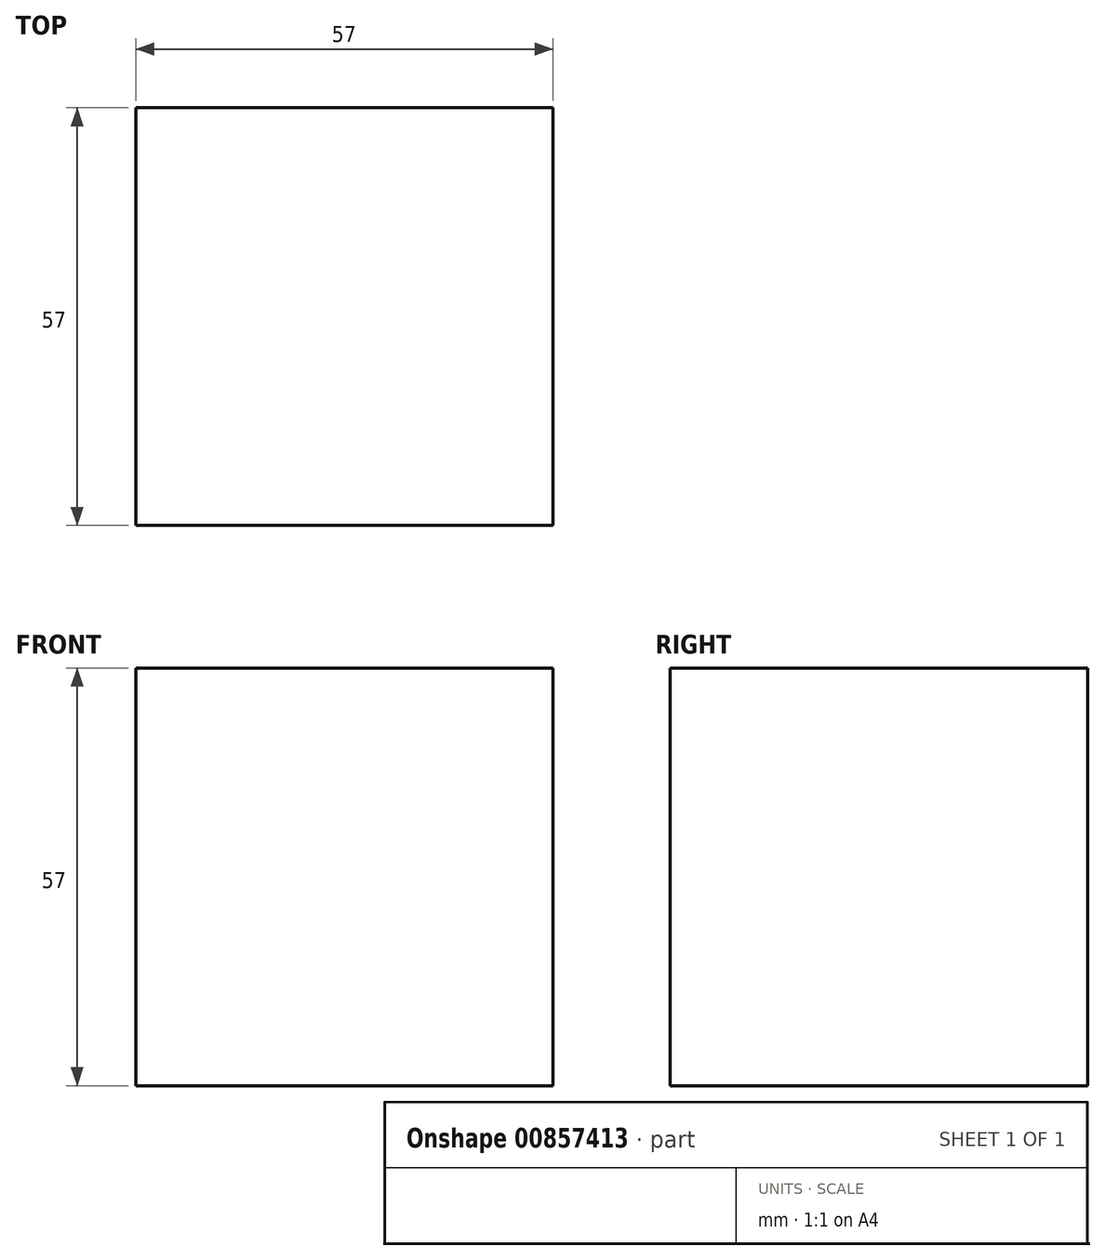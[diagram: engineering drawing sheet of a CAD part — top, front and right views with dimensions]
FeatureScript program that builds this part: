
annotation { "Feature Type Name" : "Feature", "Feature Type Description" : "" }
export const myFeature = defineFeature(function(context is Context, id is Id, definition is map)
    precondition{}
    {
        {
            var Q0;
            Q0=qCreatedBy(makeId("Front.planeOp"),FACE);
            var sketch = newSketch(context, id + "F0", { "sketchPlane" : qUnion([Q0])});
            skLineSegment(sketch, "E0", {"start": v(46.1, 88.46) * mm, "end": v(103.1, 88.46) * mm});
            skLineSegment(sketch, "E1", {"start": v(103.1, 88.46) * mm, "end": v(103.1, 31.46) * mm});
            skLineSegment(sketch, "E2", {"start": v(103.1, 31.46) * mm, "end": v(46.1, 31.46) * mm});
            skLineSegment(sketch, "E3", {"start": v(46.1, 31.46) * mm, "end": v(46.1, 88.46) * mm});
            skSolve(sketch);
        }
        {
            var Q0;
            Q0 = qSketchRegion(id + "F0", true);
            extrude(context, id + "F1", {"entities" : qUnion([Q0]), "depth" : 57 * mm, "offsetDistance" : 25 * mm});
        }
    });
